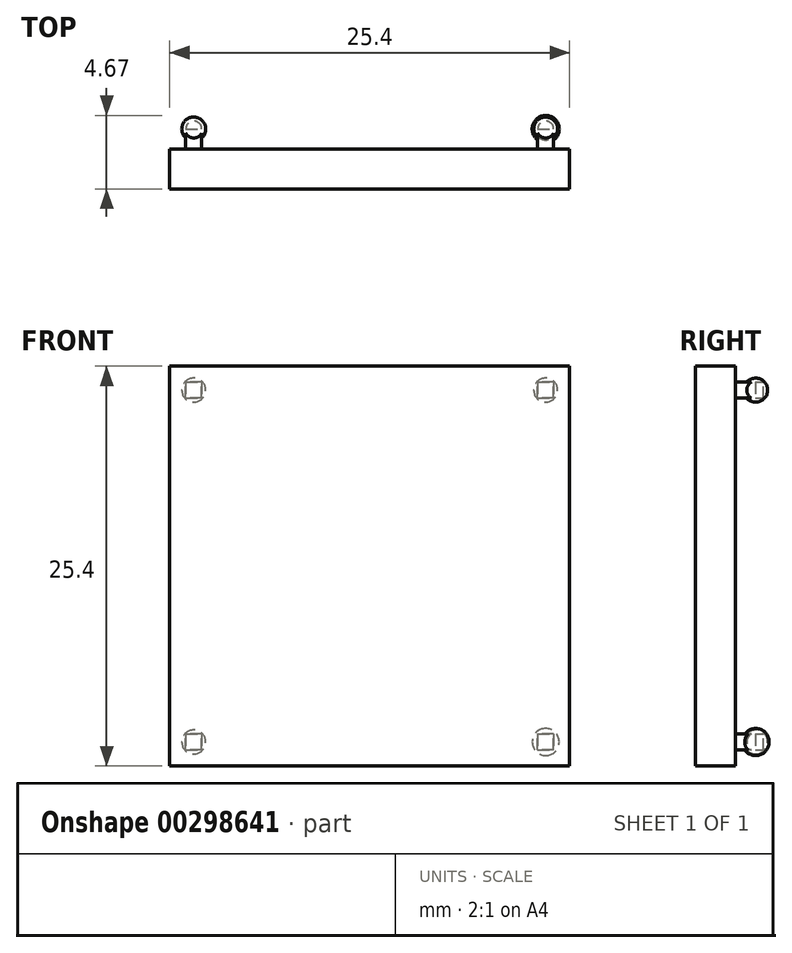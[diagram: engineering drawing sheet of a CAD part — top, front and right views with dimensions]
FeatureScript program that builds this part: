
annotation { "Feature Type Name" : "Feature", "Feature Type Description" : "" }
export const myFeature = defineFeature(function(context is Context, id is Id, definition is map)
    precondition{}
    {
        {
            var Q0;
            Q0=qCreatedBy(makeId("Front.planeOp"),FACE);
            var sketch = newSketch(context, id + "F0", { "sketchPlane" : qUnion([Q0])});
            skLineSegment(sketch, "E0.bottom", {"start": v(12.7, 12.7) * mm, "end": v(-12.7, 12.7) * mm});
            skLineSegment(sketch, "E0.top", {"start": v(12.7, -12.7) * mm, "end": v(-12.7, -12.7) * mm});
            skLineSegment(sketch, "E0.left", {"start": v(12.7, 12.7) * mm, "end": v(12.7, -12.7) * mm});
            skLineSegment(sketch, "E0.right", {"start": v(-12.7, 12.7) * mm, "end": v(-12.7, -12.7) * mm});
            skPoint(sketch, "E0.middle", {"position": v(0, 0) * mm});
            skSolve(sketch);
        }
        {
            var Q0;
            Q0=makeQuery(id+"F0.imprint","IMPRINT",FACE,{"disambiguationData":[TD([[makeQuery(id+"F0.imprint","IMPRINT",EDGE,{"derivedFrom":sQuery(id+"F0.wireOp",EDGE,"E0.bottom")}),1.0]])]});
            extrude(context, id + "F1", {"entities" : qUnion([Q0]), "depth" : 2.54 * mm});
        }
        {
            var Q0;
            Q0=makeQuery(id+"F1.opExtrude","CAP_FACE",FACE,{"disambiguationData":[OSD([sQuery(id+"F0.wireOp",EDGE,"E0.bottom"),sQuery(id+"F0.wireOp",EDGE,"E0.top"),sQuery(id+"F0.wireOp",EDGE,"E0.left"),sQuery(id+"F0.wireOp",EDGE,"E0.right")])],"isStart":true});
            var sketch = newSketch(context, id + "F2", { "sketchPlane" : qUnion([Q0])});
            skLineSegment(sketch, "E1", {"start": v(-12.7, 12.7) * mm, "end": v(-11.18, 12.7) * mm});
            skLineSegment(sketch, "E2", {"start": v(-11.18, 12.7) * mm, "end": v(-11.18, 11.18) * mm});
            skLineSegment(sketch, "E3.bottom", {"start": v(-10.67, 11.68) * mm, "end": v(-11.68, 11.68) * mm});
            skLineSegment(sketch, "E3.top", {"start": v(-10.67, 10.67) * mm, "end": v(-11.68, 10.67) * mm});
            skLineSegment(sketch, "E3.left", {"start": v(-10.67, 11.68) * mm, "end": v(-10.67, 10.67) * mm});
            skLineSegment(sketch, "E3.right", {"start": v(-11.68, 11.68) * mm, "end": v(-11.68, 10.67) * mm});
            skPoint(sketch, "E3.middle", {"position": v(-11.18, 11.18) * mm});
            skLineSegment(sketch, "E4", {"start": v(12.7, 12.7) * mm, "end": v(11.18, 12.7) * mm});
            skLineSegment(sketch, "E5", {"start": v(11.18, 12.7) * mm, "end": v(11.18, 11.18) * mm});
            skLineSegment(sketch, "E6.bottom", {"start": v(11.68, 11.68) * mm, "end": v(10.67, 11.68) * mm});
            skLineSegment(sketch, "E6.top", {"start": v(11.68, 10.67) * mm, "end": v(10.67, 10.67) * mm});
            skLineSegment(sketch, "E6.left", {"start": v(11.68, 11.68) * mm, "end": v(11.68, 10.67) * mm});
            skLineSegment(sketch, "E6.right", {"start": v(10.67, 11.68) * mm, "end": v(10.67, 10.67) * mm});
            skPoint(sketch, "E6.middle", {"position": v(11.18, 11.18) * mm});
            skLineSegment(sketch, "E7", {"start": v(-12.7, -12.7) * mm, "end": v(-11.18, -12.7) * mm});
            skLineSegment(sketch, "E8", {"start": v(-11.18, -12.7) * mm, "end": v(-11.18, -11.18) * mm});
            skLineSegment(sketch, "E9.bottom", {"start": v(-10.67, -10.67) * mm, "end": v(-11.68, -10.67) * mm});
            skLineSegment(sketch, "E9.top", {"start": v(-10.67, -11.68) * mm, "end": v(-11.68, -11.68) * mm});
            skLineSegment(sketch, "E9.left", {"start": v(-10.67, -10.67) * mm, "end": v(-10.67, -11.68) * mm});
            skLineSegment(sketch, "E9.right", {"start": v(-11.68, -10.67) * mm, "end": v(-11.68, -11.68) * mm});
            skPoint(sketch, "E9.middle", {"position": v(-11.18, -11.18) * mm});
            skLineSegment(sketch, "E10", {"start": v(12.7, -12.7) * mm, "end": v(11.18, -12.7) * mm});
            skLineSegment(sketch, "E11", {"start": v(11.18, -12.7) * mm, "end": v(11.18, -11.18) * mm});
            skPoint(sketch, "E12.middle", {"position": v(11.18, -11.18) * mm});
            skLineSegment(sketch, "E13.bottom", {"start": v(11.68, -10.67) * mm, "end": v(10.67, -10.67) * mm});
            skLineSegment(sketch, "E13.top", {"start": v(11.68, -11.68) * mm, "end": v(10.67, -11.68) * mm});
            skLineSegment(sketch, "E13.left", {"start": v(11.68, -10.67) * mm, "end": v(11.68, -11.68) * mm});
            skLineSegment(sketch, "E13.right", {"start": v(10.67, -10.67) * mm, "end": v(10.67, -11.68) * mm});
            skSolve(sketch);
        }
        {
            var Q0;
            Q0 = qSketchRegion(id + "F2", true);
            extrude(context, id + "F3", {"entities" : qUnion([Q0]), "operationType" : NewBodyOperationType.ADD, "depth" : 1.27 * mm});
        }
        {
            var Q0;
            Q0=makeQuery(id+"F3.opExtrude","CAP_FACE",FACE,{"disambiguationData":[OSD([sQuery(id+"F2.wireOp",EDGE,"E3.bottom"),sQuery(id+"F2.wireOp",EDGE,"E3.top"),sQuery(id+"F2.wireOp",EDGE,"E3.left"),sQuery(id+"F2.wireOp",EDGE,"E3.right")])],"isStart":false});
            var sketch = newSketch(context, id + "F4", { "sketchPlane" : qUnion([Q0])});
            skCircle(sketch, "E14", {"center": v(-11.18, 11.18) * mm, "radius": 0.76 * mm});
            skPoint(sketch, "E14.centerSnap0", {"position": v(-11.18, 11.68) * mm});
            skPoint(sketch, "E14.centerSnap1", {"position": v(-11.68, 11.18) * mm});
            skLineSegment(sketch, "E15", {"start": v(-11.18, 11.94) * mm, "end": v(-11.18, 10.41) * mm});
            skPoint(sketch, "E15.endSnap0", {"position": v(-11.18, 10.67) * mm});
            skSolve(sketch);
        }
        {
            var Q0;
            {var subQ0=makeQuery(id+"F3.opExtrude","CAP_EDGE",EDGE,{"disambiguationData":[OSD([sQuery(id+"F2.wireOp",EDGE,"E3.left")])],"isStart":false});Q0=makeQuery(id+"F4.imprint","IMPRINT",FACE,{"disambiguationData":[TD([[makeQuery(id+"F4.imprint","IMPRINT",EDGE,{"derivedFrom":subQ0}),1.0]])]});}
            var Q1;
            {var subQ5=makeQuery(id+"F3.opExtrude","CAP_EDGE",EDGE,{"disambiguationData":[OSD([sQuery(id+"F2.wireOp",EDGE,"E3.left")])],"isStart":false});Q1=makeQuery(id+"F4.imprint","IMPRINT",FACE,{"disambiguationData":[TD([[makeQuery(id+"F4.imprint","IMPRINT",EDGE,{"derivedFrom":subQ5}),-1.0]])]});}
            var Q2;
            {var subQ5=makeQuery(id+"F3.opExtrude","CAP_EDGE",EDGE,{"disambiguationData":[OSD([sQuery(id+"F2.wireOp",EDGE,"E3.right")])],"isStart":false});Q2=makeQuery(id+"F4.imprint","IMPRINT",FACE,{"disambiguationData":[TD([[makeQuery(id+"F4.imprint","IMPRINT",EDGE,{"derivedFrom":subQ5}),1.0]])]});}
            var Q3;
            Q3=sQuery(id+"F4.wireOp",EDGE,"E15");
            revolve(context, id + "F5", {"operationType" : NewBodyOperationType.ADD, "entities" : qUnion([Q0, Q1, Q2]), "axis" : qUnion([Q3]), "revolveType" : RevolveType.FULL});
        }
        {
            var Q0;
            Q0=makeQuery(id+"F3.opExtrude","CAP_FACE",FACE,{"disambiguationData":[OSD([sQuery(id+"F2.wireOp",EDGE,"E6.bottom"),sQuery(id+"F2.wireOp",EDGE,"E6.top"),sQuery(id+"F2.wireOp",EDGE,"E6.left"),sQuery(id+"F2.wireOp",EDGE,"E6.right")])],"isStart":false});
            var sketch = newSketch(context, id + "F6", { "sketchPlane" : qUnion([Q0])});
            skCircle(sketch, "E16", {"center": v(11.18, 11.18) * mm, "radius": 0.76 * mm});
            skPoint(sketch, "E16.centerSnap0", {"position": v(10.67, 11.18) * mm});
            skPoint(sketch, "E16.centerSnap1", {"position": v(11.18, 10.67) * mm});
            skLineSegment(sketch, "E17", {"start": v(11.18, 11.94) * mm, "end": v(11.18, 10.41) * mm});
            skPoint(sketch, "E17.startSnap0", {"position": v(11.18, 11.68) * mm});
            skSolve(sketch);
        }
        {
            var Q0;
            {var subQ0=makeQuery(id+"F3.opExtrude","CAP_EDGE",EDGE,{"disambiguationData":[OSD([sQuery(id+"F2.wireOp",EDGE,"E6.left")])],"isStart":false});Q0=makeQuery(id+"F6.imprint","IMPRINT",FACE,{"disambiguationData":[TD([[makeQuery(id+"F6.imprint","IMPRINT",EDGE,{"derivedFrom":subQ0}),1.0]])]});}
            var Q1;
            {var subQ5=makeQuery(id+"F3.opExtrude","CAP_EDGE",EDGE,{"disambiguationData":[OSD([sQuery(id+"F2.wireOp",EDGE,"E6.left")])],"isStart":false});Q1=makeQuery(id+"F6.imprint","IMPRINT",FACE,{"disambiguationData":[TD([[makeQuery(id+"F6.imprint","IMPRINT",EDGE,{"derivedFrom":subQ5}),-1.0]])]});}
            var Q2;
            {var subQ5=makeQuery(id+"F3.opExtrude","CAP_EDGE",EDGE,{"disambiguationData":[OSD([sQuery(id+"F2.wireOp",EDGE,"E6.right")])],"isStart":false});Q2=makeQuery(id+"F6.imprint","IMPRINT",FACE,{"disambiguationData":[TD([[makeQuery(id+"F6.imprint","IMPRINT",EDGE,{"derivedFrom":subQ5}),1.0]])]});}
            var Q3;
            Q3=sQuery(id+"F6.wireOp",EDGE,"E17");
            revolve(context, id + "F7", {"operationType" : NewBodyOperationType.ADD, "entities" : qUnion([Q0, Q1, Q2]), "axis" : qUnion([Q3]), "revolveType" : RevolveType.FULL});
        }
        {
            var Q0;
            Q0=makeQuery(id+"F3.opExtrude","CAP_FACE",FACE,{"disambiguationData":[OSD([sQuery(id+"F2.wireOp",EDGE,"E13.bottom"),sQuery(id+"F2.wireOp",EDGE,"E13.top"),sQuery(id+"F2.wireOp",EDGE,"E13.left"),sQuery(id+"F2.wireOp",EDGE,"E13.right")])],"isStart":false});
            var sketch = newSketch(context, id + "F8", { "sketchPlane" : qUnion([Q0])});
            skCircle(sketch, "E18", {"center": v(11.18, -11.18) * mm, "radius": 0.76 * mm});
            skPoint(sketch, "E18.centerSnap0", {"position": v(11.68, -11.18) * mm});
            skPoint(sketch, "E18.centerSnap1", {"position": v(11.18, -10.67) * mm});
            skLineSegment(sketch, "E19", {"start": v(11.18, -10.41) * mm, "end": v(11.18, -11.94) * mm});
            skPoint(sketch, "E19.endSnap0", {"position": v(11.18, -11.68) * mm});
            skSolve(sketch);
        }
        {
            var Q0;
            {var subQ0=makeQuery(id+"F3.opExtrude","CAP_EDGE",EDGE,{"disambiguationData":[OSD([sQuery(id+"F2.wireOp",EDGE,"E13.left")])],"isStart":false});Q0=makeQuery(id+"F8.imprint","IMPRINT",FACE,{"disambiguationData":[TD([[makeQuery(id+"F8.imprint","IMPRINT",EDGE,{"derivedFrom":subQ0}),1.0]])]});}
            var Q1;
            {var subQ5=makeQuery(id+"F3.opExtrude","CAP_EDGE",EDGE,{"disambiguationData":[OSD([sQuery(id+"F2.wireOp",EDGE,"E13.left")])],"isStart":false});Q1=makeQuery(id+"F8.imprint","IMPRINT",FACE,{"disambiguationData":[TD([[makeQuery(id+"F8.imprint","IMPRINT",EDGE,{"derivedFrom":subQ5}),-1.0]])]});}
            var Q2;
            {var subQ5=makeQuery(id+"F3.opExtrude","CAP_EDGE",EDGE,{"disambiguationData":[OSD([sQuery(id+"F2.wireOp",EDGE,"E13.right")])],"isStart":false});Q2=makeQuery(id+"F8.imprint","IMPRINT",FACE,{"disambiguationData":[TD([[makeQuery(id+"F8.imprint","IMPRINT",EDGE,{"derivedFrom":subQ5}),1.0]])]});}
            var Q3;
            Q3=sQuery(id+"F8.wireOp",EDGE,"E19");
            revolve(context, id + "F9", {"operationType" : NewBodyOperationType.ADD, "entities" : qUnion([Q0, Q1, Q2]), "axis" : qUnion([Q3]), "revolveType" : RevolveType.FULL});
        }
        {
            var Q0;
            Q0=makeQuery(id+"F3.opExtrude","CAP_FACE",FACE,{"disambiguationData":[OSD([sQuery(id+"F2.wireOp",EDGE,"E9.bottom"),sQuery(id+"F2.wireOp",EDGE,"E9.top"),sQuery(id+"F2.wireOp",EDGE,"E9.left"),sQuery(id+"F2.wireOp",EDGE,"E9.right")])],"isStart":false});
            var sketch = newSketch(context, id + "F10", { "sketchPlane" : qUnion([Q0])});
            skPoint(sketch, "E20.centerSnap0", {"position": v(-10.67, -11.18) * mm});
            skPoint(sketch, "E20.centerSnap1", {"position": v(-11.18, -10.67) * mm});
            skCircle(sketch, "E21", {"center": v(-11.18, -11.18) * mm, "radius": 0.86 * mm});
            skLineSegment(sketch, "E22", {"start": v(-11.18, -10.32) * mm, "end": v(-11.18, -12.03) * mm});
            skSolve(sketch);
        }
        {
            var Q0;
            {var subQ0=makeQuery(id+"F3.opExtrude","CAP_EDGE",EDGE,{"disambiguationData":[OSD([sQuery(id+"F2.wireOp",EDGE,"E9.right")])],"isStart":false});Q0=makeQuery(id+"F10.imprint","IMPRINT",FACE,{"disambiguationData":[TD([[makeQuery(id+"F10.imprint","IMPRINT",EDGE,{"derivedFrom":subQ0}),-1.0]])]});}
            var Q1;
            {var subQ5=makeQuery(id+"F3.opExtrude","CAP_EDGE",EDGE,{"disambiguationData":[OSD([sQuery(id+"F2.wireOp",EDGE,"E9.left")])],"isStart":false});Q1=makeQuery(id+"F10.imprint","IMPRINT",FACE,{"disambiguationData":[TD([[makeQuery(id+"F10.imprint","IMPRINT",EDGE,{"derivedFrom":subQ5}),-1.0]])]});}
            var Q2;
            {var subQ5=makeQuery(id+"F3.opExtrude","CAP_EDGE",EDGE,{"disambiguationData":[OSD([sQuery(id+"F2.wireOp",EDGE,"E9.right")])],"isStart":false});Q2=makeQuery(id+"F10.imprint","IMPRINT",FACE,{"disambiguationData":[TD([[makeQuery(id+"F10.imprint","IMPRINT",EDGE,{"derivedFrom":subQ5}),1.0]])]});}
            var Q3;
            Q3=sQuery(id+"F10.wireOp",EDGE,"E22");
            revolve(context, id + "F11", {"operationType" : NewBodyOperationType.ADD, "entities" : qUnion([Q0, Q1, Q2]), "axis" : qUnion([Q3]), "revolveType" : RevolveType.FULL});
        }
    });
